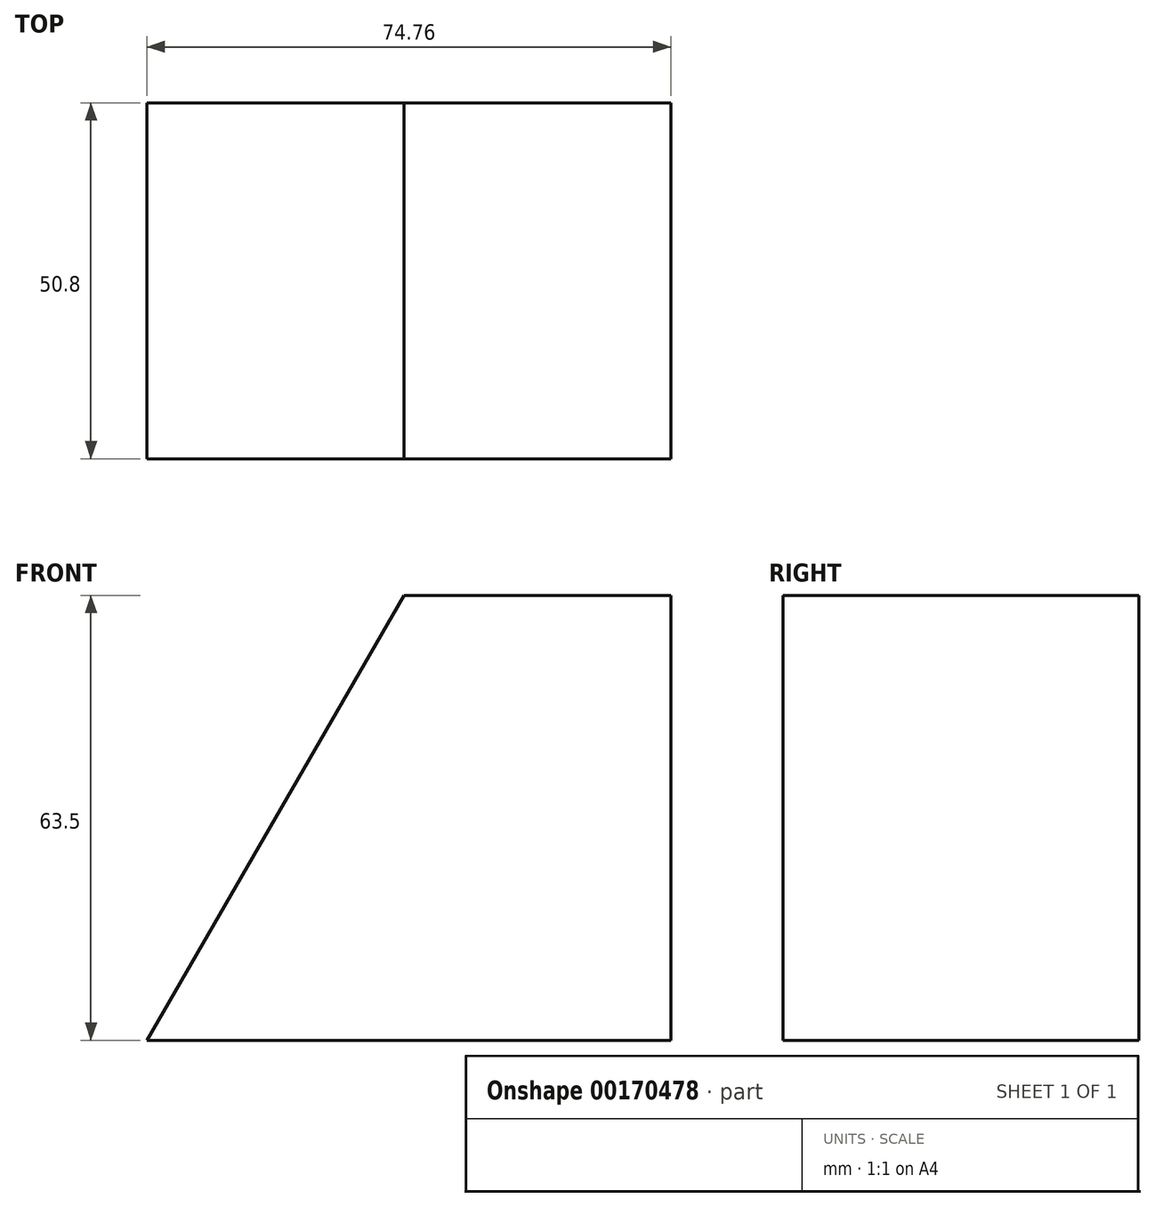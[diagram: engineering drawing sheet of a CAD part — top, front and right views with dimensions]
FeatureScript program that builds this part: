
annotation { "Feature Type Name" : "Feature", "Feature Type Description" : "" }
export const myFeature = defineFeature(function(context is Context, id is Id, definition is map)
    precondition{}
    {
        {
            var Q0;
            Q0=qCreatedBy(makeId("Front.planeOp"),FACE);
            var sketch = newSketch(context, id + "F0", { "sketchPlane" : qUnion([Q0])});
            skLineSegment(sketch, "E0.bottom", {"start": v(19.05, 0) * mm, "end": v(-19.05, 0) * mm});
            skLineSegment(sketch, "E0.top", {"start": v(19.05, 63.5) * mm, "end": v(-19.05, 63.5) * mm});
            skLineSegment(sketch, "E0.left", {"start": v(19.05, 0) * mm, "end": v(19.05, 63.5) * mm});
            skLineSegment(sketch, "E0.right", {"start": v(-19.05, 0) * mm, "end": v(-19.05, 63.5) * mm});
            skPoint(sketch, "E0.middle", {"position": v(0, 31.75) * mm});
            skSolve(sketch);
        }
        {
            var Q0;
            Q0=makeQuery(id+"F0.imprint","IMPRINT",FACE,{"disambiguationData":[TD([[makeQuery(id+"F0.imprint","IMPRINT",EDGE,{"derivedFrom":sQuery(id+"F0.wireOp",EDGE,"E0.bottom")}),-1.0]])]});
            extrude(context, id + "F1", {"entities" : qUnion([Q0]), "depth" : 50.8 * mm, "offsetDistance" : 25.4 * mm, "symmetric" : true});
        }
        {
            var Q0;
            Q0=makeQuery(id+"F1.opExtrude","CAP_FACE",FACE,{"disambiguationData":[OSD([sQuery(id+"F0.wireOp",EDGE,"E0.bottom"),sQuery(id+"F0.wireOp",EDGE,"E0.top"),sQuery(id+"F0.wireOp",EDGE,"E0.left"),sQuery(id+"F0.wireOp",EDGE,"E0.right")])],"isStart":false});
            var sketch = newSketch(context, id + "F2", { "sketchPlane" : qUnion([Q0])});
            skLineSegment(sketch, "E1", {"start": v(-19.05, 63.5) * mm, "end": v(-55.71, 0) * mm});
            skLineSegment(sketch, "E2", {"start": v(-55.71, 0) * mm, "end": v(-19.05, 0) * mm});
            skLineSegment(sketch, "E3", {"start": v(-19.05, 0) * mm, "end": v(-19.05, 63.5) * mm});
            skSolve(sketch);
        }
        {
            var Q0;
            Q0=makeQuery(id+"F2.imprint","IMPRINT",FACE,{"disambiguationData":[TD([[makeQuery(id+"F2.imprint","IMPRINT",EDGE,{"derivedFrom":sQuery(id+"F2.wireOp",EDGE,"E1")}),1.0]])]});
            var Q1;
            Q1=makeQuery(id+"F1.opExtrude","CAP_FACE",FACE,{"disambiguationData":[OSD([sQuery(id+"F0.wireOp",EDGE,"E0.bottom"),sQuery(id+"F0.wireOp",EDGE,"E0.top"),sQuery(id+"F0.wireOp",EDGE,"E0.left"),sQuery(id+"F0.wireOp",EDGE,"E0.right")])],"isStart":true});
            extrude(context, id + "F3", {"entities" : qUnion([Q0]), "operationType" : NewBodyOperationType.ADD, "endBound" : BoundingType.UP_TO_SURFACE, "oppositeDirection" : true, "depth" : 25.4 * mm, "endBoundEntityFace" : qUnion([Q1]), "offsetDistance" : 25.4 * mm});
        }
    });
